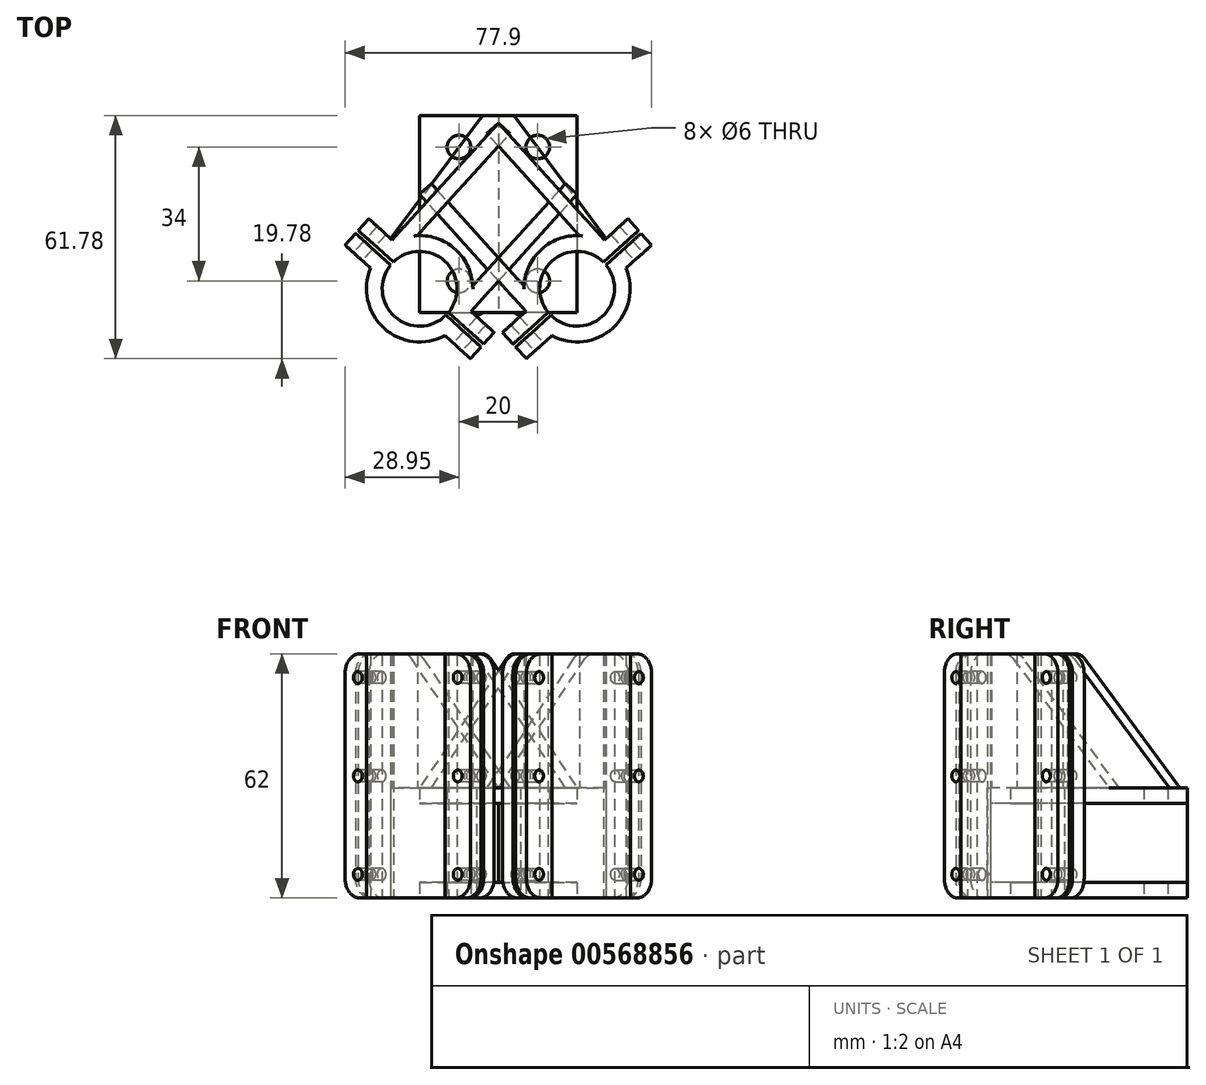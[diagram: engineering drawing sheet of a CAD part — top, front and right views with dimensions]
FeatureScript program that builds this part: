
annotation { "Feature Type Name" : "Feature", "Feature Type Description" : "" }
export const myFeature = defineFeature(function(context is Context, id is Id, definition is map)
    precondition{}
    {
        {
            var Q0;
            Q0=qCreatedBy(makeId("Top.planeOp"),FACE);
            var sketch = newSketch(context, id + "F0", { "sketchPlane" : qUnion([Q0])});
            skLineSegment(sketch, "E0", {"start": v(-66.6, 0) * mm, "end": v(72.2, 0) * mm, "construction": true});
            skLineSegment(sketch, "E1", {"start": v(0, 0) * mm, "end": v(0, 88.22) * mm, "construction": true});
            skLineSegment(sketch, "E2", {"start": v(20, 88.34) * mm, "end": v(20, 0) * mm, "construction": true});
            skCircle(sketch, "E3", {"center": v(-20, 6) * mm, "radius": 5 * mm, "construction": true});
            skCircle(sketch, "E4", {"center": v(-20, 6) * mm, "radius": 9.5 * mm});
            skLineSegment(sketch, "E5", {"start": v(0, 50) * mm, "end": v(0, 0) * mm});
            skLineSegment(sketch, "E6", {"start": v(0, 0) * mm, "end": v(-4, 0) * mm});
            skLineSegment(sketch, "E7", {"start": v(-4, 0) * mm, "end": v(-4, 50) * mm});
            skLineSegment(sketch, "E8", {"start": v(-4, 50) * mm, "end": v(0, 50) * mm});
            skLineSegment(sketch, "E9", {"start": v(0, 50) * mm, "end": v(20, 50) * mm});
            skLineSegment(sketch, "E10", {"start": v(20, 50) * mm, "end": v(20, 0) * mm});
            skLineSegment(sketch, "E11", {"start": v(20, 0) * mm, "end": v(0, 0) * mm});
            skCircle(sketch, "E12", {"center": v(-20, 6) * mm, "radius": 13.5 * mm});
            skLineSegment(sketch, "E13", {"start": v(-12.92, -5.5) * mm, "end": v(-4, 0) * mm});
            skLineSegment(sketch, "E14", {"start": v(-4, 50) * mm, "end": v(-30.82, 14.08) * mm});
            skLineSegment(sketch, "E15", {"start": v(10, 50) * mm, "end": v(10, 0) * mm, "construction": true});
            skCircle(sketch, "E16", {"center": v(10, 8) * mm, "radius": 3 * mm});
            skCircle(sketch, "E17", {"center": v(10, 42) * mm, "radius": 3 * mm});
            skSolve(sketch);
        }
        {
            var Q0;
            Q0 = qSketchRegion(id + "F0", true);
            extrude(context, id + "F1", {"entities" : qUnion([Q0]), "depth" : 28 * mm, "offsetDistance" : 25 * mm});
        }
        {
            var Q0;
            Q0=makeQuery(id+"F0.imprint","IMPRINT",FACE,{"disambiguationData":[TD([[makeQuery(id+"F0.imprint","IMPRINT",EDGE,{"derivedFrom":sQuery(id+"F0.wireOp",EDGE,"E4")}),-1.0]])]});
            extrude(context, id + "F2", {"entities" : qUnion([Q0]), "operationType" : NewBodyOperationType.ADD, "depth" : 62 * mm, "offsetDistance" : 25 * mm});
        }
        {
            var Q0;
            Q0=qCreatedBy(makeId("Top.planeOp"),FACE);
            var sketch = newSketch(context, id + "F3", { "sketchPlane" : qUnion([Q0])});
            skCircle(sketch, "E18.0", {"center": v(-20, 6) * mm, "radius": 13.5 * mm, "construction": true});
            skLineSegment(sketch, "E18.1", {"start": v(-4, 50) * mm, "end": v(-30.82, 14.08) * mm, "construction": true});
            skLineSegment(sketch, "E18.2", {"start": v(-12.92, -5.5) * mm, "end": v(-4, 0) * mm, "construction": true});
            skLineSegment(sketch, "E18.3", {"start": v(20, 0) * mm, "end": v(-4, 0) * mm, "construction": true});
            skLineSegment(sketch, "E18.6", {"start": v(-4, 50) * mm, "end": v(20, 50) * mm, "construction": true});
            skLineSegment(sketch, "E18.7", {"start": v(20, 50) * mm, "end": v(20, 0) * mm, "construction": true});
            skLineSegment(sketch, "E19.0", {"start": v(-4, 0) * mm, "end": v(-4, 50) * mm, "construction": true});
            skCircle(sketch, "E20.0", {"center": v(-20, 6) * mm, "radius": 9.5 * mm, "construction": true});
            skLineSegment(sketch, "E21.bottom", {"start": v(-12.96, -0.38) * mm, "end": v(17.04, 32.7) * mm});
            skLineSegment(sketch, "E21.top", {"start": v(-10, -3.07) * mm, "end": v(20, 30) * mm});
            skLineSegment(sketch, "E21.left", {"start": v(-12.96, -0.38) * mm, "end": v(-10, -3.07) * mm});
            skLineSegment(sketch, "E21.right", {"start": v(17.04, 32.7) * mm, "end": v(20, 30) * mm});
            skCircle(sketch, "E22", {"center": v(10, 8) * mm, "radius": 6 * mm, "construction": true});
            skLineSegment(sketch, "E23.bottom", {"start": v(0, 48.15) * mm, "end": v(2.96, 45.46) * mm});
            skLineSegment(sketch, "E23.top", {"start": v(-30, 15.07) * mm, "end": v(-27.04, 12.38) * mm});
            skLineSegment(sketch, "E23.left", {"start": v(0, 48.15) * mm, "end": v(-30, 15.07) * mm});
            skLineSegment(sketch, "E23.right", {"start": v(2.96, 45.46) * mm, "end": v(-27.04, 12.38) * mm});
            skCircle(sketch, "E24", {"center": v(10, 42) * mm, "radius": 6 * mm, "construction": true});
            skCircle(sketch, "E25.0", {"center": v(10, 42) * mm, "radius": 3 * mm, "construction": true});
            skCircle(sketch, "E25.1", {"center": v(10, 8) * mm, "radius": 3 * mm, "construction": true});
            skSolve(sketch);
        }
        {
            var Q0;
            Q0 = qSketchRegion(id + "F3", true);
            extrude(context, id + "F4", {"entities" : qUnion([Q0]), "operationType" : NewBodyOperationType.ADD, "depth" : 62 * mm, "offsetDistance" : 25 * mm});
        }
        {
            var Q0;
            Q0=makeQuery(id+"F0.imprint","IMPRINT",FACE,{"disambiguationData":[TD([[makeQuery(id+"F0.imprint","IMPRINT",EDGE,{"derivedFrom":sQuery(id+"F0.wireOp",EDGE,"E5")}),1.0]])]});
            extrude(context, id + "F5", {"entities" : qUnion([Q0]), "operationType" : NewBodyOperationType.REMOVE, "depth" : 24 * mm, "offsetDistance" : 25 * mm, "hasSecondDirection" : true, "secondDirectionOppositeDirection" : false, "secondDirectionDepth" : 4 * mm});
        }
        {
            var Q0;
            Q0=makeQuery(id+"F4.opExtrude","CAP_EDGE",EDGE,{"disambiguationData":[OSD([sQuery(id+"F3.wireOp",EDGE,"E21.right")])],"isStart":false});
            var Q1;
            Q1=makeQuery(id+"F4.opExtrude","CAP_EDGE",EDGE,{"disambiguationData":[OSD([sQuery(id+"F3.wireOp",EDGE,"E23.bottom")])],"isStart":false});
            chamfer(context, id + "F6", {"entities" : qUnion([Q0, Q1]), "width" : 34 * mm, "tangentPropagation" : true});
        }
        {
            var Q0;
            {var subQ0=sQuery(id+"F3.wireOp",EDGE,"E21.right");Q0=makeQuery(id+"F6.opChamfer","BLEND_EDGE",EDGE,{"blendedFrom":[makeQuery(id+"F4.opExtrude","CAP_EDGE",EDGE,{"disambiguationData":[OSD([subQ0])],"isStart":false}),makeQuery(id+"F4.boolean.opBoolean","MERGE",FACE,{"derivedFrom":[makeQuery(id+"F2.opExtrude","CAP_FACE",FACE,{"disambiguationData":[OSD([sQuery(id+"F0.wireOp",EDGE,"E4"),sQuery(id+"F0.wireOp",EDGE,"E12")])],"isStart":false}),makeQuery(id+"F4.opExtrude","CAP_FACE",FACE,{"disambiguationData":[OSD([sQuery(id+"F3.wireOp",EDGE,"E21.bottom"),sQuery(id+"F3.wireOp",EDGE,"E21.top"),sQuery(id+"F3.wireOp",EDGE,"E21.left"),subQ0])],"isStart":false}),makeQuery(id+"F4.opExtrude","CAP_FACE",FACE,{"disambiguationData":[OSD([sQuery(id+"F3.wireOp",EDGE,"E23.bottom"),sQuery(id+"F3.wireOp",EDGE,"E23.top"),sQuery(id+"F3.wireOp",EDGE,"E23.left"),sQuery(id+"F3.wireOp",EDGE,"E23.right")])],"isStart":false})]})],"blendedInto":[makeQuery(id+"F4.boolean.opBoolean","MERGE",FACE,{"derivedFrom":[makeQuery(id+"F2.opExtrude","CAP_FACE",FACE,{"disambiguationData":[OSD([sQuery(id+"F0.wireOp",EDGE,"E4"),sQuery(id+"F0.wireOp",EDGE,"E12")])],"isStart":false}),makeQuery(id+"F4.opExtrude","CAP_FACE",FACE,{"disambiguationData":[OSD([sQuery(id+"F3.wireOp",EDGE,"E21.bottom"),sQuery(id+"F3.wireOp",EDGE,"E21.top"),sQuery(id+"F3.wireOp",EDGE,"E21.left"),subQ0])],"isStart":false}),makeQuery(id+"F4.opExtrude","CAP_FACE",FACE,{"disambiguationData":[OSD([sQuery(id+"F3.wireOp",EDGE,"E23.bottom"),sQuery(id+"F3.wireOp",EDGE,"E23.top"),sQuery(id+"F3.wireOp",EDGE,"E23.left"),sQuery(id+"F3.wireOp",EDGE,"E23.right")])],"isStart":false})]})]});}
            var Q1;
            {var subQ0=sQuery(id+"F3.wireOp",EDGE,"E23.bottom");Q1=makeQuery(id+"F6.opChamfer","BLEND_EDGE",EDGE,{"blendedFrom":[makeQuery(id+"F4.opExtrude","CAP_EDGE",EDGE,{"disambiguationData":[OSD([subQ0])],"isStart":false}),makeQuery(id+"F4.boolean.opBoolean","MERGE",FACE,{"derivedFrom":[makeQuery(id+"F2.opExtrude","CAP_FACE",FACE,{"disambiguationData":[OSD([sQuery(id+"F0.wireOp",EDGE,"E4"),sQuery(id+"F0.wireOp",EDGE,"E12")])],"isStart":false}),makeQuery(id+"F4.opExtrude","CAP_FACE",FACE,{"disambiguationData":[OSD([sQuery(id+"F3.wireOp",EDGE,"E21.bottom"),sQuery(id+"F3.wireOp",EDGE,"E21.top"),sQuery(id+"F3.wireOp",EDGE,"E21.left"),sQuery(id+"F3.wireOp",EDGE,"E21.right")])],"isStart":false}),makeQuery(id+"F4.opExtrude","CAP_FACE",FACE,{"disambiguationData":[OSD([subQ0,sQuery(id+"F3.wireOp",EDGE,"E23.top"),sQuery(id+"F3.wireOp",EDGE,"E23.left"),sQuery(id+"F3.wireOp",EDGE,"E23.right")])],"isStart":false})]})],"blendedInto":[makeQuery(id+"F4.boolean.opBoolean","MERGE",FACE,{"derivedFrom":[makeQuery(id+"F2.opExtrude","CAP_FACE",FACE,{"disambiguationData":[OSD([sQuery(id+"F0.wireOp",EDGE,"E4"),sQuery(id+"F0.wireOp",EDGE,"E12")])],"isStart":false}),makeQuery(id+"F4.opExtrude","CAP_FACE",FACE,{"disambiguationData":[OSD([sQuery(id+"F3.wireOp",EDGE,"E21.bottom"),sQuery(id+"F3.wireOp",EDGE,"E21.top"),sQuery(id+"F3.wireOp",EDGE,"E21.left"),sQuery(id+"F3.wireOp",EDGE,"E21.right")])],"isStart":false}),makeQuery(id+"F4.opExtrude","CAP_FACE",FACE,{"disambiguationData":[OSD([subQ0,sQuery(id+"F3.wireOp",EDGE,"E23.top"),sQuery(id+"F3.wireOp",EDGE,"E23.left"),sQuery(id+"F3.wireOp",EDGE,"E23.right")])],"isStart":false})]})]});}
            fillet(context, id + "F7", {"entities" : qUnion([Q0, Q1]), "radius" : 4 * mm, "tangentPropagation" : true, "allowEdgeOverflow" : false});
        }
        {
            var Q0;
            Q0=qCreatedBy(makeId("Top.planeOp"),FACE);
            var sketch = newSketch(context, id + "F8", { "sketchPlane" : qUnion([Q0])});
            skCircle(sketch, "E26.0", {"center": v(-20, 6) * mm, "radius": 13.5 * mm, "construction": true});
            skCircle(sketch, "E26.1", {"center": v(-20, 6) * mm, "radius": 9.5 * mm, "construction": true});
            skLineSegment(sketch, "E26.2", {"start": v(-10, -3.07) * mm, "end": v(20, 30) * mm, "construction": true});
            skLineSegment(sketch, "E26.3", {"start": v(0, 48.15) * mm, "end": v(-30, 15.07) * mm, "construction": true});
            skLineSegment(sketch, "E27", {"start": v(-42.23, 26.16) * mm, "end": v(3.9, -15.68) * mm, "construction": true});
            skLineSegment(sketch, "E28", {"start": v(-31.54, 10.4) * mm, "end": v(-38.95, 17.11) * mm});
            skLineSegment(sketch, "E29", {"start": v(-36.26, 20.07) * mm, "end": v(-25.9, 10.67) * mm});
            skLineSegment(sketch, "E30", {"start": v(-20, 6) * mm, "end": v(-44.9, -21.45) * mm, "construction": true});
            skLineSegment(sketch, "E31", {"start": v(-31.54, 10.4) * mm, "end": v(-28.85, 13.36) * mm});
            skLineSegment(sketch, "E32.MirrorCS", {"start": v(-35.6, 20.81) * mm, "end": v(-25.22, 11.4) * mm});
            skLineSegment(sketch, "E33.MirrorCS", {"start": v(-25.5, 17.06) * mm, "end": v(-28.18, 14.1) * mm});
            skLineSegment(sketch, "E34.MirrorCS", {"start": v(-25.5, 17.06) * mm, "end": v(-32.9, 23.78) * mm});
            skLineSegment(sketch, "E35", {"start": v(-38.95, 17.11) * mm, "end": v(-32.9, 23.78) * mm});
            skLineSegment(sketch, "E36", {"start": v(-25.9, 10.67) * mm, "end": v(-25.22, 11.4) * mm});
            skLineSegment(sketch, "E37.MirrorCS", {"start": v(-14.5, -5.06) * mm, "end": v(-7.1, -11.78) * mm});
            skLineSegment(sketch, "E38.MirrorCS", {"start": v(-14.5, -5.06) * mm, "end": v(-11.82, -2.1) * mm});
            skLineSegment(sketch, "E39.MirrorCS", {"start": v(-4.4, -8.81) * mm, "end": v(-14.78, 0.6) * mm});
            skLineSegment(sketch, "E40.MirrorCS", {"start": v(-3.74, -8.07) * mm, "end": v(-14.1, 1.33) * mm});
            skLineSegment(sketch, "E41.MirrorCS", {"start": v(-8.46, 1.6) * mm, "end": v(-11.15, -1.36) * mm});
            skLineSegment(sketch, "E42.MirrorCS", {"start": v(-8.46, 1.6) * mm, "end": v(-1.05, -5.11) * mm});
            skLineSegment(sketch, "E43.MirrorCS", {"start": v(-7.1, -11.78) * mm, "end": v(-1.05, -5.11) * mm});
            skLineSegment(sketch, "E44.MirrorCS", {"start": v(-14.78, 0.6) * mm, "end": v(-14.1, 1.33) * mm});
            skSolve(sketch);
        }
        {
            var Q0;
            {var subQ0=sQuery(id+"F8.wireOp",EDGE,"E28");Q0=makeQuery(id+"F8.imprint","IMPRINT",FACE,{"disambiguationData":[TD([[makeQuery(id+"F8.imprint","IMPRINT",EDGE,{"derivedFrom":subQ0}),-1.0]])]});}
            var Q1;
            {var subQ3=sQuery(id+"F8.wireOp",EDGE,"E33.MirrorCS");Q1=makeQuery(id+"F8.imprint","IMPRINT",FACE,{"disambiguationData":[TD([[makeQuery(id+"F8.imprint","IMPRINT",EDGE,{"derivedFrom":subQ3}),-1.0]])]});}
            var Q2;
            {var subQ0=sQuery(id+"F8.wireOp",EDGE,"E37.MirrorCS");Q2=makeQuery(id+"F8.imprint","IMPRINT",FACE,{"disambiguationData":[TD([[makeQuery(id+"F8.imprint","IMPRINT",EDGE,{"derivedFrom":subQ0}),1.0]])]});}
            var Q3;
            {var subQ3=sQuery(id+"F8.wireOp",EDGE,"E41.MirrorCS");Q3=makeQuery(id+"F8.imprint","IMPRINT",FACE,{"disambiguationData":[TD([[makeQuery(id+"F8.imprint","IMPRINT",EDGE,{"derivedFrom":subQ3}),1.0]])]});}
            extrude(context, id + "F9", {"entities" : qUnion([Q0, Q1, Q2, Q3]), "operationType" : NewBodyOperationType.ADD, "depth" : 62 * mm, "offsetDistance" : 25 * mm});
        }
        {
            var Q0;
            {var subQ0=sQuery(id+"F8.wireOp",EDGE,"E36");Q0=makeQuery(id+"F8.imprint","IMPRINT",FACE,{"disambiguationData":[TD([[makeQuery(id+"F8.imprint","IMPRINT",EDGE,{"derivedFrom":subQ0}),1.0]])]});}
            var Q1;
            {var subQ0=sQuery(id+"F8.wireOp",EDGE,"E44.MirrorCS");Q1=makeQuery(id+"F8.imprint","IMPRINT",FACE,{"disambiguationData":[TD([[makeQuery(id+"F8.imprint","IMPRINT",EDGE,{"derivedFrom":subQ0}),-1.0]])]});}
            extrude(context, id + "F10", {"entities" : qUnion([Q0, Q1]), "operationType" : NewBodyOperationType.REMOVE, "depth" : 62 * mm, "offsetDistance" : 25 * mm});
        }
        {
            var Q0;
            Q0=makeQuery(id+"F9.opExtrude","SWEPT_FACE",FACE,{"disambiguationData":[OSD([sQuery(id+"F8.wireOp",EDGE,"E28")])]});
            var sketch = newSketch(context, id + "F11", { "sketchPlane" : qUnion([Q0])});
            skLineSegment(sketch, "E45.0", {"start": v(-40.35, 62) * mm, "end": v(-40.35, 0) * mm, "construction": true});
            skLineSegment(sketch, "E45.1", {"start": v(-31.57, 62) * mm, "end": v(-31.57, 0) * mm, "construction": true});
            skLineSegment(sketch, "E45.2", {"start": v(-6.12, 62) * mm, "end": v(-6.12, 0) * mm, "construction": true});
            skLineSegment(sketch, "E45.3", {"start": v(2.65, 62) * mm, "end": v(2.65, 0) * mm, "construction": true});
            skLineSegment(sketch, "E45.4", {"start": v(-6.12, 62) * mm, "end": v(2.65, 62) * mm, "construction": true});
            skLineSegment(sketch, "E45.5", {"start": v(-31.57, 62) * mm, "end": v(-40.35, 62) * mm, "construction": true});
            skLineSegment(sketch, "E45.6", {"start": v(-31.57, 0) * mm, "end": v(-40.35, 0) * mm, "construction": true});
            skLineSegment(sketch, "E45.7", {"start": v(-6.12, 0) * mm, "end": v(2.65, 0) * mm, "construction": true});
            skLineSegment(sketch, "E46", {"start": v(-35.96, 62) * mm, "end": v(-35.96, 0) * mm, "construction": true});
            skLineSegment(sketch, "E47", {"start": v(-1.73, 0) * mm, "end": v(-1.73, 62) * mm, "construction": true});
            skLineSegment(sketch, "E48", {"start": v(-35.96, 56) * mm, "end": v(-1.73, 56) * mm, "construction": true});
            skLineSegment(sketch, "E49", {"start": v(-1.73, 31) * mm, "end": v(-35.96, 31) * mm, "construction": true});
            skLineSegment(sketch, "E50", {"start": v(-35.96, 6) * mm, "end": v(-1.73, 6) * mm, "construction": true});
            skCircle(sketch, "E51", {"center": v(-35.96, 56) * mm, "radius": 1.5 * mm});
            skCircle(sketch, "E52", {"center": v(-35.96, 56) * mm, "radius": 1.25 * mm});
            skCircle(sketch, "E53", {"center": v(-1.73, 56) * mm, "radius": 1.5 * mm});
            skCircle(sketch, "E54", {"center": v(-1.73, 56) * mm, "radius": 1.25 * mm});
            skCircle(sketch, "E55", {"center": v(-1.73, 31) * mm, "radius": 1.5 * mm});
            skCircle(sketch, "E56", {"center": v(-1.73, 31) * mm, "radius": 1.25 * mm});
            skCircle(sketch, "E57", {"center": v(-35.96, 31) * mm, "radius": 1.5 * mm});
            skCircle(sketch, "E58", {"center": v(-35.96, 31) * mm, "radius": 1.25 * mm});
            skCircle(sketch, "E59", {"center": v(-35.96, 6) * mm, "radius": 1.5 * mm});
            skCircle(sketch, "E60", {"center": v(-35.96, 6) * mm, "radius": 1.25 * mm});
            skCircle(sketch, "E61", {"center": v(-1.73, 6) * mm, "radius": 1.5 * mm});
            skCircle(sketch, "E62", {"center": v(-1.73, 6) * mm, "radius": 1.25 * mm});
            skSolve(sketch);
        }
        {
            var Q0;
            Q0=makeQuery(id+"F11.imprint","IMPRINT",FACE,{"disambiguationData":[TD([[makeQuery(id+"F11.imprint","IMPRINT",EDGE,{"derivedFrom":sQuery(id+"F11.wireOp",EDGE,"E51")}),1.0]])]});
            var Q1;
            Q1=makeQuery(id+"F11.imprint","IMPRINT",FACE,{"disambiguationData":[TD([[makeQuery(id+"F11.imprint","IMPRINT",EDGE,{"derivedFrom":sQuery(id+"F11.wireOp",EDGE,"E52")}),1.0]])]});
            var Q2;
            Q2=makeQuery(id+"F11.imprint","IMPRINT",FACE,{"disambiguationData":[TD([[makeQuery(id+"F11.imprint","IMPRINT",EDGE,{"derivedFrom":sQuery(id+"F11.wireOp",EDGE,"E53")}),1.0]])]});
            var Q3;
            Q3=makeQuery(id+"F11.imprint","IMPRINT",FACE,{"disambiguationData":[TD([[makeQuery(id+"F11.imprint","IMPRINT",EDGE,{"derivedFrom":sQuery(id+"F11.wireOp",EDGE,"E54")}),1.0]])]});
            var Q4;
            Q4=makeQuery(id+"F11.imprint","IMPRINT",FACE,{"disambiguationData":[TD([[makeQuery(id+"F11.imprint","IMPRINT",EDGE,{"derivedFrom":sQuery(id+"F11.wireOp",EDGE,"E57")}),1.0]])]});
            var Q5;
            Q5=makeQuery(id+"F11.imprint","IMPRINT",FACE,{"disambiguationData":[TD([[makeQuery(id+"F11.imprint","IMPRINT",EDGE,{"derivedFrom":sQuery(id+"F11.wireOp",EDGE,"E58")}),1.0]])]});
            var Q6;
            Q6=makeQuery(id+"F11.imprint","IMPRINT",FACE,{"disambiguationData":[TD([[makeQuery(id+"F11.imprint","IMPRINT",EDGE,{"derivedFrom":sQuery(id+"F11.wireOp",EDGE,"E55")}),1.0]])]});
            var Q7;
            Q7=makeQuery(id+"F11.imprint","IMPRINT",FACE,{"disambiguationData":[TD([[makeQuery(id+"F11.imprint","IMPRINT",EDGE,{"derivedFrom":sQuery(id+"F11.wireOp",EDGE,"E56")}),1.0]])]});
            var Q8;
            Q8=makeQuery(id+"F11.imprint","IMPRINT",FACE,{"disambiguationData":[TD([[makeQuery(id+"F11.imprint","IMPRINT",EDGE,{"derivedFrom":sQuery(id+"F11.wireOp",EDGE,"E61")}),1.0]])]});
            var Q9;
            Q9=makeQuery(id+"F11.imprint","IMPRINT",FACE,{"disambiguationData":[TD([[makeQuery(id+"F11.imprint","IMPRINT",EDGE,{"derivedFrom":sQuery(id+"F11.wireOp",EDGE,"E62")}),1.0]])]});
            var Q10;
            Q10=makeQuery(id+"F11.imprint","IMPRINT",FACE,{"disambiguationData":[TD([[makeQuery(id+"F11.imprint","IMPRINT",EDGE,{"derivedFrom":sQuery(id+"F11.wireOp",EDGE,"E59")}),1.0]])]});
            var Q11;
            Q11=makeQuery(id+"F11.imprint","IMPRINT",FACE,{"disambiguationData":[TD([[makeQuery(id+"F11.imprint","IMPRINT",EDGE,{"derivedFrom":sQuery(id+"F11.wireOp",EDGE,"E60")}),1.0]])]});
            extrude(context, id + "F12", {"entities" : qUnion([Q0, Q1, Q2, Q3, Q4, Q5, Q6, Q7, Q8, Q9, Q10, Q11]), "operationType" : NewBodyOperationType.REMOVE, "oppositeDirection" : true, "depth" : 10 * mm, "offsetDistance" : 25 * mm});
        }
        {
            var Q0;
            Q0=makeQuery(id+"F11.imprint","IMPRINT",FACE,{"disambiguationData":[TD([[makeQuery(id+"F11.imprint","IMPRINT",EDGE,{"derivedFrom":sQuery(id+"F11.wireOp",EDGE,"E60")}),1.0]])]});
            var Q1;
            Q1=makeQuery(id+"F11.imprint","IMPRINT",FACE,{"disambiguationData":[TD([[makeQuery(id+"F11.imprint","IMPRINT",EDGE,{"derivedFrom":sQuery(id+"F11.wireOp",EDGE,"E58")}),1.0]])]});
            var Q2;
            Q2=makeQuery(id+"F11.imprint","IMPRINT",FACE,{"disambiguationData":[TD([[makeQuery(id+"F11.imprint","IMPRINT",EDGE,{"derivedFrom":sQuery(id+"F11.wireOp",EDGE,"E62")}),1.0]])]});
            var Q3;
            Q3=makeQuery(id+"F11.imprint","IMPRINT",FACE,{"disambiguationData":[TD([[makeQuery(id+"F11.imprint","IMPRINT",EDGE,{"derivedFrom":sQuery(id+"F11.wireOp",EDGE,"E56")}),1.0]])]});
            var Q4;
            Q4=makeQuery(id+"F11.imprint","IMPRINT",FACE,{"disambiguationData":[TD([[makeQuery(id+"F11.imprint","IMPRINT",EDGE,{"derivedFrom":sQuery(id+"F11.wireOp",EDGE,"E54")}),1.0]])]});
            var Q5;
            Q5=makeQuery(id+"F11.imprint","IMPRINT",FACE,{"disambiguationData":[TD([[makeQuery(id+"F11.imprint","IMPRINT",EDGE,{"derivedFrom":sQuery(id+"F11.wireOp",EDGE,"E52")}),1.0]])]});
            extrude(context, id + "F13", {"entities" : qUnion([Q0, Q1, Q2, Q3, Q4, Q5]), "operationType" : NewBodyOperationType.REMOVE, "oppositeDirection" : true, "depth" : 10 * mm, "offsetDistance" : 25 * mm});
        }
        {
            var Q0;
            {var subQ0=sQuery(id+"F8.wireOp",EDGE,"E43.MirrorCS");Q0=makeQuery(id+"F9.opExtrude","CAP_EDGE",EDGE,{"disambiguationData":[OSD([subQ0]),TDD([makeQuery(id+"F8.imprint","IMPRINT",EDGE,{"disambiguationData":[TD([[makeQuery(id+"F8.imprint","INTERSECT",VERTEX,{"derivedFrom":[sQuery(id+"F8.wireOp",EDGE,"E37.MirrorCS"),subQ0]}),-1.0]])],"derivedFrom":subQ0})])],"isStart":false});}
            var Q1;
            {var subQ0=sQuery(id+"F8.wireOp",EDGE,"E43.MirrorCS");Q1=makeQuery(id+"F9.opExtrude","CAP_EDGE",EDGE,{"disambiguationData":[OSD([subQ0]),TDD([makeQuery(id+"F8.imprint","IMPRINT",EDGE,{"disambiguationData":[TD([[makeQuery(id+"F8.imprint","INTERSECT",VERTEX,{"derivedFrom":[sQuery(id+"F8.wireOp",EDGE,"E40.MirrorCS"),subQ0]}),-1.0]])],"derivedFrom":subQ0})])],"isStart":false});}
            var Q2;
            {var subQ0=sQuery(id+"F8.wireOp",EDGE,"E43.MirrorCS");Q2=makeQuery(id+"F9.opExtrude","CAP_EDGE",EDGE,{"disambiguationData":[OSD([subQ0]),TDD([makeQuery(id+"F8.imprint","IMPRINT",EDGE,{"disambiguationData":[TD([[makeQuery(id+"F8.imprint","INTERSECT",VERTEX,{"derivedFrom":[sQuery(id+"F8.wireOp",EDGE,"E37.MirrorCS"),subQ0]}),-1.0]])],"derivedFrom":subQ0})])],"isStart":true});}
            var Q3;
            {var subQ0=sQuery(id+"F8.wireOp",EDGE,"E43.MirrorCS");Q3=makeQuery(id+"F9.opExtrude","CAP_EDGE",EDGE,{"disambiguationData":[OSD([subQ0]),TDD([makeQuery(id+"F8.imprint","IMPRINT",EDGE,{"disambiguationData":[TD([[makeQuery(id+"F8.imprint","INTERSECT",VERTEX,{"derivedFrom":[sQuery(id+"F8.wireOp",EDGE,"E40.MirrorCS"),subQ0]}),-1.0]])],"derivedFrom":subQ0})])],"isStart":true});}
            var Q4;
            {var subQ0=sQuery(id+"F8.wireOp",EDGE,"E35");Q4=makeQuery(id+"F9.opExtrude","CAP_EDGE",EDGE,{"disambiguationData":[OSD([subQ0]),TDD([makeQuery(id+"F8.imprint","IMPRINT",EDGE,{"disambiguationData":[TD([[makeQuery(id+"F8.imprint","INTERSECT",VERTEX,{"derivedFrom":[sQuery(id+"F8.wireOp",EDGE,"E28"),subQ0]}),-1.0]])],"derivedFrom":subQ0})])],"isStart":true});}
            var Q5;
            {var subQ0=sQuery(id+"F8.wireOp",EDGE,"E35");Q5=makeQuery(id+"F9.opExtrude","CAP_EDGE",EDGE,{"disambiguationData":[OSD([subQ0]),TDD([makeQuery(id+"F8.imprint","IMPRINT",EDGE,{"disambiguationData":[TD([[makeQuery(id+"F8.imprint","INTERSECT",VERTEX,{"derivedFrom":[sQuery(id+"F8.wireOp",EDGE,"E32.MirrorCS"),subQ0]}),-1.0]])],"derivedFrom":subQ0})])],"isStart":true});}
            var Q6;
            {var subQ0=sQuery(id+"F8.wireOp",EDGE,"E35");Q6=makeQuery(id+"F9.opExtrude","CAP_EDGE",EDGE,{"disambiguationData":[OSD([subQ0]),TDD([makeQuery(id+"F8.imprint","IMPRINT",EDGE,{"disambiguationData":[TD([[makeQuery(id+"F8.imprint","INTERSECT",VERTEX,{"derivedFrom":[sQuery(id+"F8.wireOp",EDGE,"E28"),subQ0]}),-1.0]])],"derivedFrom":subQ0})])],"isStart":false});}
            var Q7;
            {var subQ0=sQuery(id+"F8.wireOp",EDGE,"E35");Q7=makeQuery(id+"F9.opExtrude","CAP_EDGE",EDGE,{"disambiguationData":[OSD([subQ0]),TDD([makeQuery(id+"F8.imprint","IMPRINT",EDGE,{"disambiguationData":[TD([[makeQuery(id+"F8.imprint","INTERSECT",VERTEX,{"derivedFrom":[sQuery(id+"F8.wireOp",EDGE,"E32.MirrorCS"),subQ0]}),-1.0]])],"derivedFrom":subQ0})])],"isStart":false});}
            fillet(context, id + "F14", {"entities" : qUnion([Q0, Q1, Q2, Q3, Q4, Q5, Q6, Q7]), "radius" : 5 * mm, "tangentPropagation" : true, "allowEdgeOverflow" : false});
        }
        {
            var Q0;
            Q0=makeQuery(id+"F10.boolean.opBoolean","SPLIT",BODY,{"disambiguationData":[OD(0.0)],"derivedFrom":makeQuery(id+"F1.opExtrude","SWEPT_BODY",BODY,{"disambiguationData":[OSD([sQuery(id+"F0.wireOp",EDGE,"E4"),sQuery(id+"F0.wireOp",EDGE,"E6"),sQuery(id+"F0.wireOp",EDGE,"E8"),sQuery(id+"F0.wireOp",EDGE,"E9"),sQuery(id+"F0.wireOp",EDGE,"E10"),sQuery(id+"F0.wireOp",EDGE,"E11"),sQuery(id+"F0.wireOp",EDGE,"E12"),sQuery(id+"F0.wireOp",EDGE,"E13"),sQuery(id+"F0.wireOp",EDGE,"E14"),sQuery(id+"F0.wireOp",EDGE,"E16"),sQuery(id+"F0.wireOp",EDGE,"E17")])]})});
            var Q1;
            Q1=qCreatedBy(makeId("Right.planeOp"),FACE);
            mirror(context, id + "F15", {"entities" : qUnion([Q0]), "mirrorPlane" : qUnion([Q1])});
        }
    });
